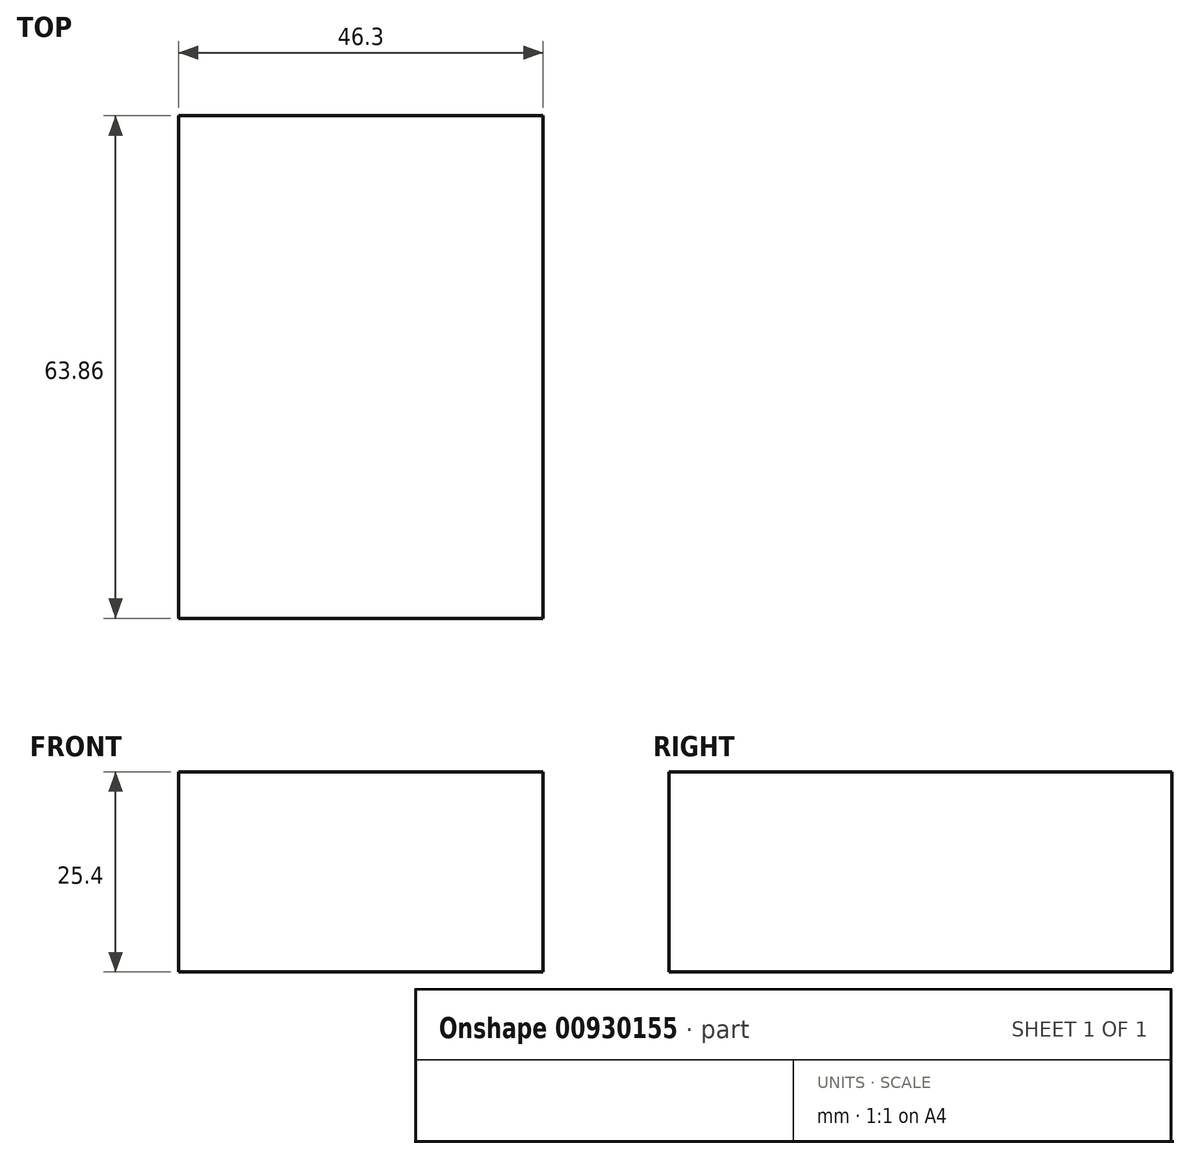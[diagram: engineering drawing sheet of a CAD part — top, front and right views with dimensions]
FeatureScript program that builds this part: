
annotation { "Feature Type Name" : "Feature", "Feature Type Description" : "" }
export const myFeature = defineFeature(function(context is Context, id is Id, definition is map)
    precondition{}
    {
        {
            var Q0;
            Q0=qCreatedBy(makeId("Top.planeOp"),FACE);
            var sketch = newSketch(context, id + "F0", { "sketchPlane" : qUnion([Q0])});
            skLineSegment(sketch, "E0.bottom", {"start": v(-23.15, 31.93) * mm, "end": v(23.15, 31.93) * mm});
            skLineSegment(sketch, "E0.top", {"start": v(-23.15, -31.93) * mm, "end": v(23.15, -31.93) * mm});
            skLineSegment(sketch, "E0.left", {"start": v(-23.15, 31.93) * mm, "end": v(-23.15, -31.93) * mm});
            skLineSegment(sketch, "E0.right", {"start": v(23.15, 31.93) * mm, "end": v(23.15, -31.93) * mm});
            skPoint(sketch, "E0.middle", {"position": v(0, 0) * mm});
            skSolve(sketch);
        }
        {
            var Q0;
            Q0=makeQuery(id+"F0.imprint","IMPRINT",FACE,{"disambiguationData":[TD([[makeQuery(id+"F0.imprint","IMPRINT",EDGE,{"derivedFrom":sQuery(id+"F0.wireOp",EDGE,"E0.bottom")}),-1.0]])]});
            extrude(context, id + "F1", {"entities" : qUnion([Q0]), "depth" : 25.4 * mm, "offsetDistance" : 25.4 * mm});
        }
    });
